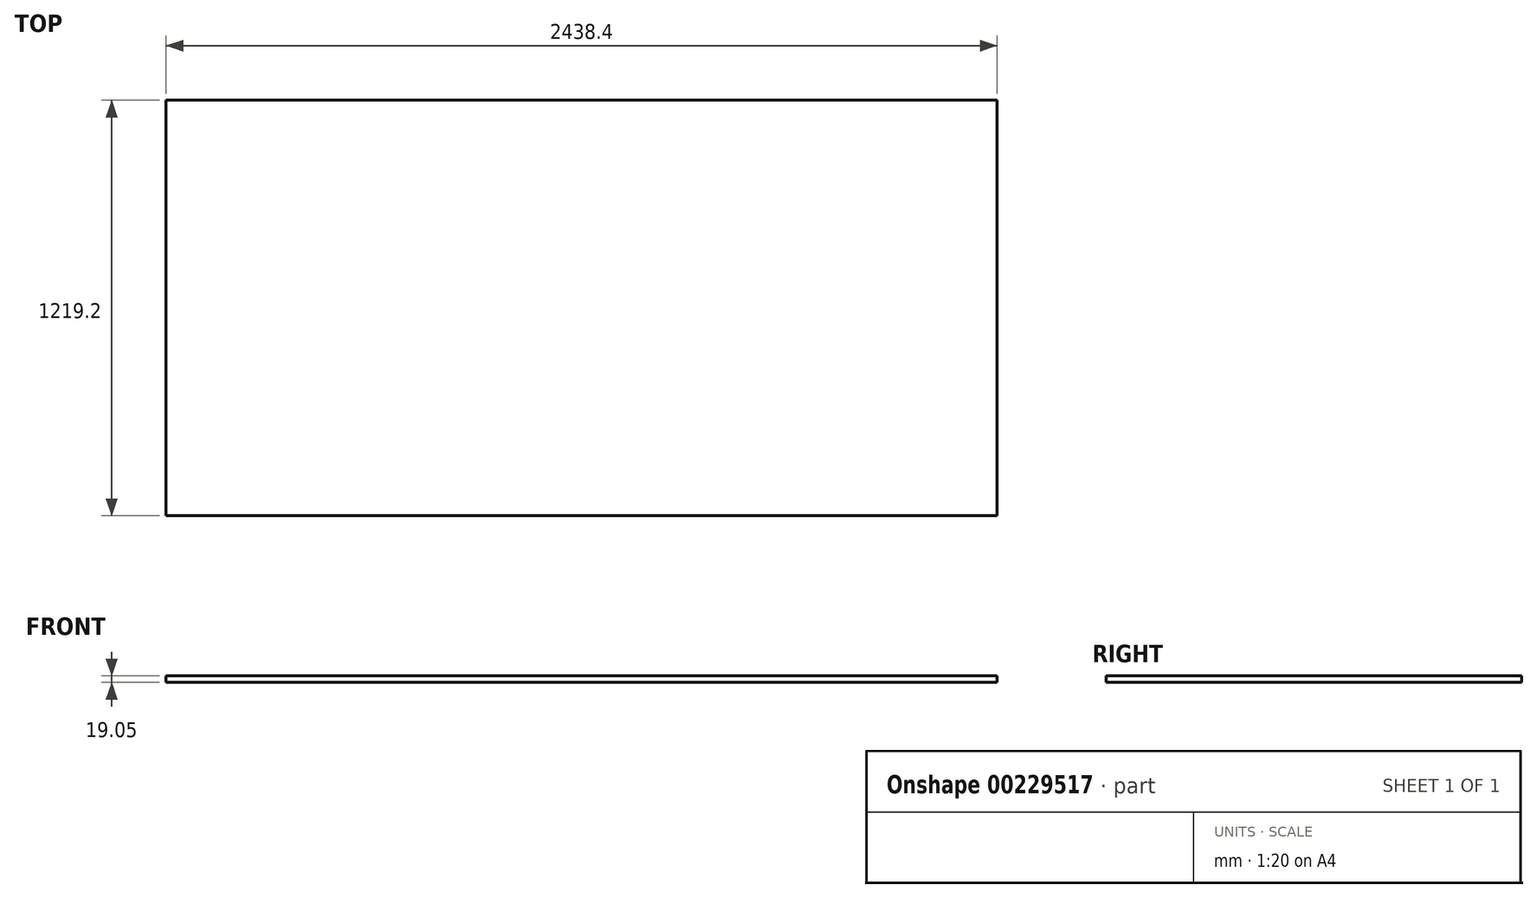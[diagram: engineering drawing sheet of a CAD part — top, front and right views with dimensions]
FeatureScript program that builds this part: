
annotation { "Feature Type Name" : "Feature", "Feature Type Description" : "" }
export const myFeature = defineFeature(function(context is Context, id is Id, definition is map)
    precondition{}
    {
        {
            var Q0;
            Q0=qCreatedBy(makeId("Top.planeOp"),FACE);
            var sketch = newSketch(context, id + "F0", { "sketchPlane" : qUnion([Q0])});
            skLineSegment(sketch, "E0.bottom", {"start": v(0, 0) * mm, "end": v(2438.4, 0) * mm});
            skLineSegment(sketch, "E0.top", {"start": v(0, -1219.2) * mm, "end": v(2438.4, -1219.2) * mm});
            skLineSegment(sketch, "E0.left", {"start": v(0, 0) * mm, "end": v(0, -1219.2) * mm});
            skLineSegment(sketch, "E0.right", {"start": v(2438.4, 0) * mm, "end": v(2438.4, -1219.2) * mm});
            skSolve(sketch);
        }
        {
            var Q0;
            Q0=makeQuery(id+"F0.imprint","IMPRINT",FACE,{"disambiguationData":[TD([[makeQuery(id+"F0.imprint","IMPRINT",EDGE,{"derivedFrom":sQuery(id+"F0.wireOp",EDGE,"E0.bottom")}),-1.0]])]});
            extrude(context, id + "F1", {"entities" : qUnion([Q0]), "depth" : 19.05 * mm});
        }
    });
